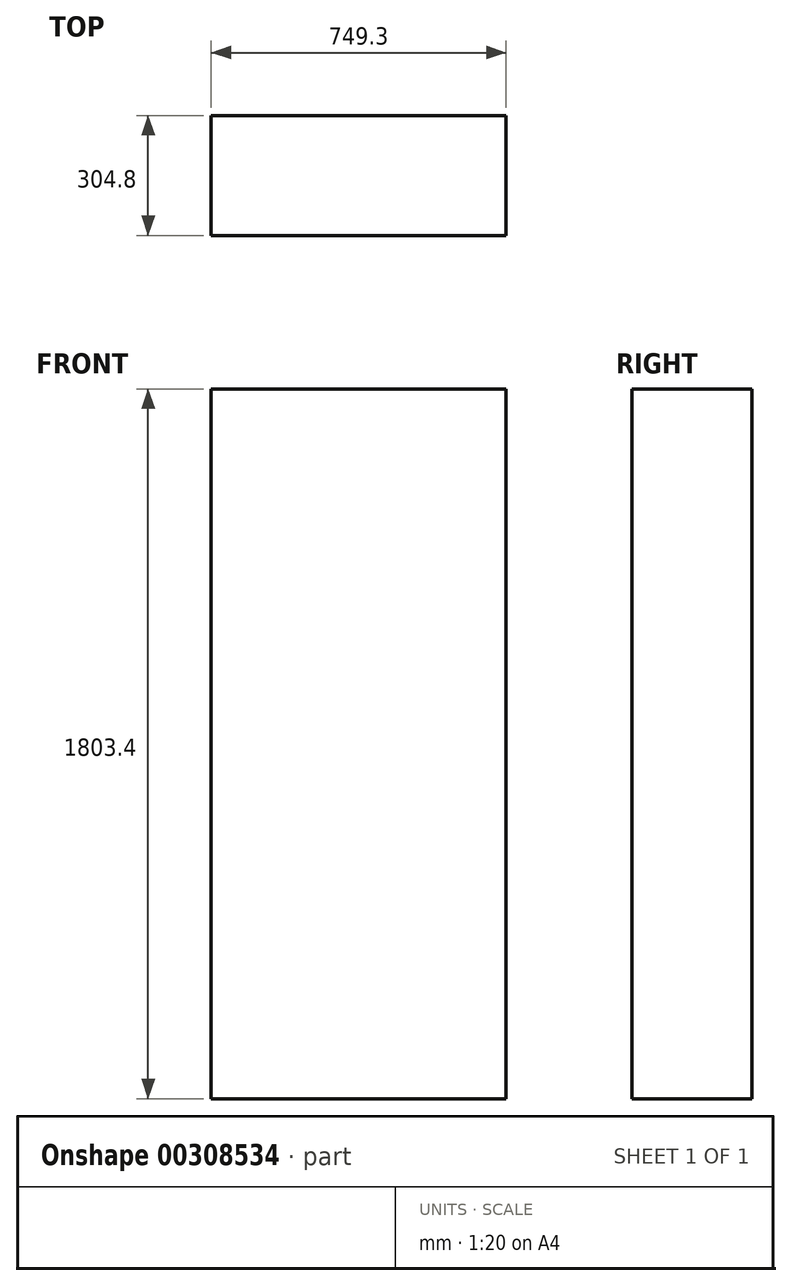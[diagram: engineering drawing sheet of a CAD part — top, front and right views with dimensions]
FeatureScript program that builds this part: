
annotation { "Feature Type Name" : "Feature", "Feature Type Description" : "" }
export const myFeature = defineFeature(function(context is Context, id is Id, definition is map)
    precondition{}
    {
        {
            var Q0;
            Q0=qCreatedBy(makeId("Top.planeOp"),FACE);
            var sketch = newSketch(context, id + "F0", { "sketchPlane" : qUnion([Q0])});
            skLineSegment(sketch, "E0.bottom", {"start": v(374.65, -152.4) * mm, "end": v(-374.65, -152.4) * mm});
            skLineSegment(sketch, "E0.top", {"start": v(374.65, 152.4) * mm, "end": v(-374.65, 152.4) * mm});
            skLineSegment(sketch, "E0.left", {"start": v(374.65, -152.4) * mm, "end": v(374.65, 152.4) * mm});
            skLineSegment(sketch, "E0.right", {"start": v(-374.65, -152.4) * mm, "end": v(-374.65, 152.4) * mm});
            skPoint(sketch, "E0.middle", {"position": v(0, 0) * mm});
            skSolve(sketch);
        }
        {
            var Q0;
            Q0=makeQuery(id+"F0.imprint","IMPRINT",FACE,{"disambiguationData":[TD([[makeQuery(id+"F0.imprint","IMPRINT",EDGE,{"derivedFrom":sQuery(id+"F0.wireOp",EDGE,"E0.bottom")}),-1.0]])]});
            extrude(context, id + "F1", {"entities" : qUnion([Q0]), "depth" : 1803.4 * mm});
        }
    });
